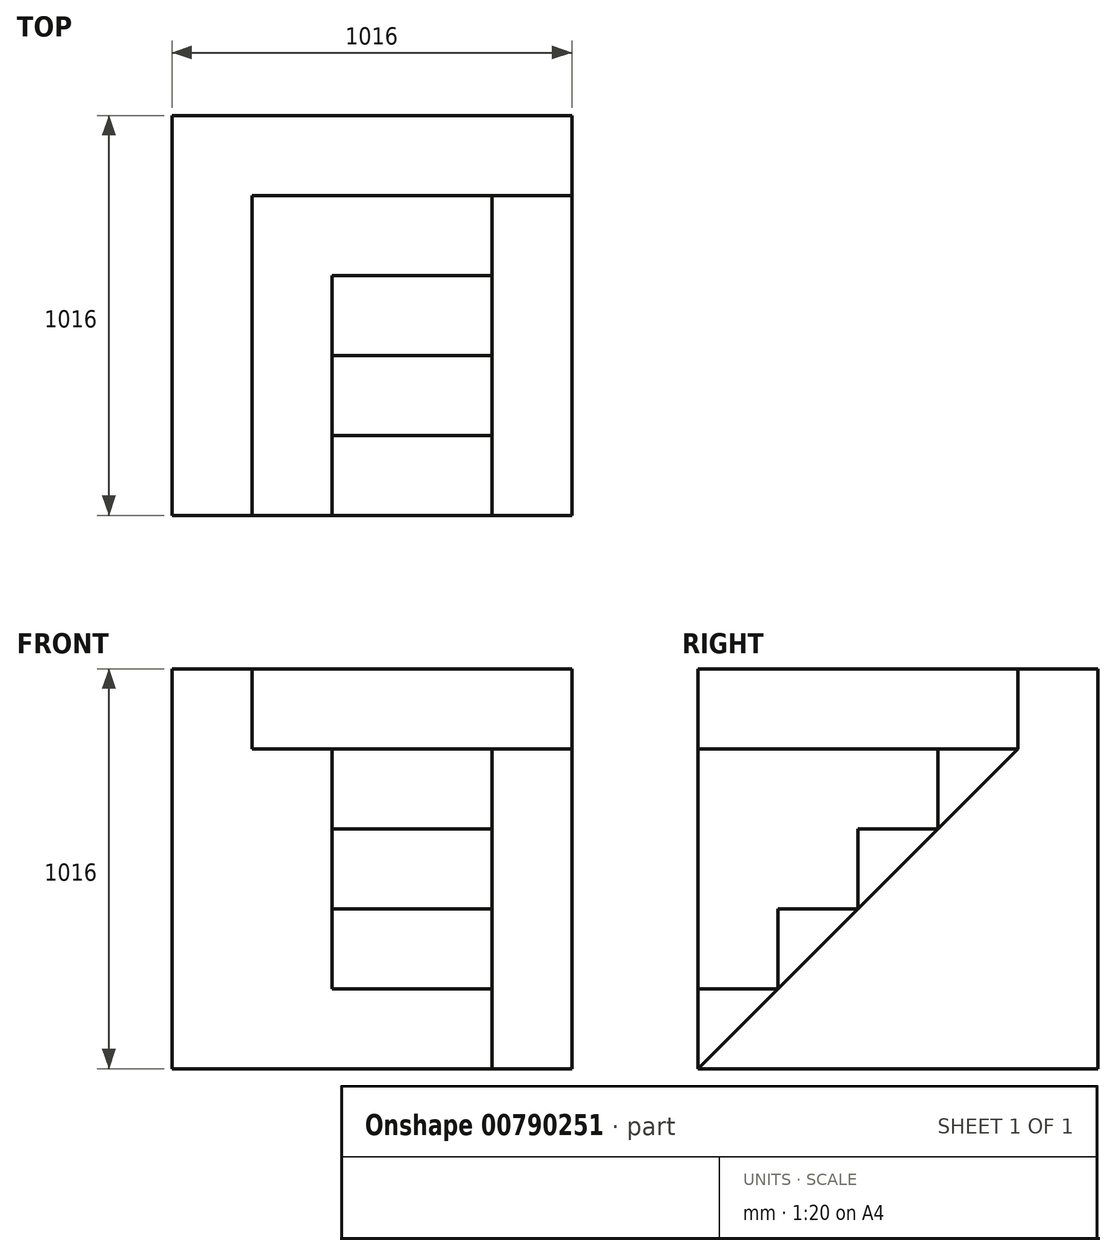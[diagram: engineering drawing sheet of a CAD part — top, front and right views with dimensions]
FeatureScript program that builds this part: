
annotation { "Feature Type Name" : "Feature", "Feature Type Description" : "" }
export const myFeature = defineFeature(function(context is Context, id is Id, definition is map)
    precondition{}
    {
        {
            var Q0;
            Q0=qCreatedBy(makeId("Top.planeOp"),FACE);
            var sketch = newSketch(context, id + "F0", { "sketchPlane" : qUnion([Q0])});
            skLineSegment(sketch, "E0.bottom", {"start": v(-508, -508) * mm, "end": v(508, -508) * mm});
            skLineSegment(sketch, "E0.top", {"start": v(-508, 508) * mm, "end": v(508, 508) * mm});
            skLineSegment(sketch, "E0.left", {"start": v(-508, -508) * mm, "end": v(-508, 508) * mm});
            skLineSegment(sketch, "E0.right", {"start": v(508, -508) * mm, "end": v(508, 508) * mm});
            skLineSegment(sketch, "E1", {"start": v(-304.8, 304.8) * mm, "end": v(-304.8, -508) * mm});
            skLineSegment(sketch, "E2", {"start": v(-304.8, 304.8) * mm, "end": v(508, 304.8) * mm});
            skLineSegment(sketch, "E3", {"start": v(304.8, 304.8) * mm, "end": v(304.8, -508) * mm});
            skLineSegment(sketch, "E4", {"start": v(304.8, 101.6) * mm, "end": v(-101.6, 101.6) * mm});
            skLineSegment(sketch, "E5", {"start": v(-101.6, -101.6) * mm, "end": v(304.8, -101.6) * mm});
            skLineSegment(sketch, "E6", {"start": v(-101.6, -304.8) * mm, "end": v(304.8, -304.8) * mm});
            skLineSegment(sketch, "E7.trimOffspring", {"start": v(-101.6, 101.6) * mm, "end": v(-101.6, -508) * mm});
            skSolve(sketch);
        }
        {
            var Q0;
            {var subQ1=sQuery(id+"F0.wireOp",EDGE,"E0.right");var subQ6=sQuery(id+"F0.wireOp",EDGE,"E0.bottom");var subQ7=makeQuery(id+"F0.imprint","INTERSECT",VERTEX,{"derivedFrom":[subQ6,subQ1]});Q0=makeQuery(id+"F0.imprint","IMPRINT",FACE,{"disambiguationData":[TD([[makeQuery(id+"F0.imprint","IMPRINT",EDGE,{"disambiguationData":[TD([[subQ7,1.0]])],"derivedFrom":subQ6}),1.0]])]});}
            extrude(context, id + "F1", {"entities" : qUnion([Q0]), "depth" : 812.8 * mm, "offsetDistance" : 25.4 * mm});
        }
        {
            var Q0;
            Q0=makeQuery(id+"F1.opExtrude","SWEPT_FACE",FACE,{"disambiguationData":[OSD([sQuery(id+"F0.wireOp",EDGE,"E0.right")])]});
            var sketch = newSketch(context, id + "F2", { "sketchPlane" : qUnion([Q0])});
            skLineSegment(sketch, "E8", {"start": v(-508, 0) * mm, "end": v(304.8, 812.8) * mm});
            skSolve(sketch);
        }
        {
            var Q0;
            Q0=makeQuery(id+"F2.imprint","IMPRINT",FACE,{"disambiguationData":[TD([[makeQuery(id+"F2.imprint","IMPRINT",EDGE,{"derivedFrom":sQuery(id+"F2.wireOp",EDGE,"E8")}),1.0]])]});
            extrude(context, id + "F3", {"entities" : qUnion([Q0]), "operationType" : NewBodyOperationType.REMOVE, "oppositeDirection" : true, "depth" : 16916.4 * mm, "offsetDistance" : 25.4 * mm});
        }
        {
            var Q0;
            {var subQ1=sQuery(id+"F0.wireOp",EDGE,"E0.top");Q0=makeQuery(id+"F0.imprint","IMPRINT",FACE,{"disambiguationData":[TD([[makeQuery(id+"F0.imprint","IMPRINT",EDGE,{"derivedFrom":subQ1}),-1.0]])]});}
            extrude(context, id + "F4", {"entities" : qUnion([Q0]), "operationType" : NewBodyOperationType.ADD, "depth" : 1016 * mm, "offsetDistance" : 25.4 * mm});
        }
        {
            var Q0;
            {var subQ1=sQuery(id+"F0.wireOp",EDGE,"E1");Q0=makeQuery(id+"F0.imprint","IMPRINT",FACE,{"disambiguationData":[TD([[makeQuery(id+"F0.imprint","IMPRINT",EDGE,{"derivedFrom":subQ1}),1.0]])]});}
            extrude(context, id + "F5", {"entities" : qUnion([Q0]), "operationType" : NewBodyOperationType.ADD, "depth" : 812.8 * mm, "offsetDistance" : 25.4 * mm});
        }
        {
            var Q0;
            {var subQ0=sQuery(id+"F0.wireOp",EDGE,"E4");Q0=makeQuery(id+"F0.imprint","IMPRINT",FACE,{"disambiguationData":[TD([[makeQuery(id+"F0.imprint","IMPRINT",EDGE,{"derivedFrom":subQ0}),1.0]])]});}
            extrude(context, id + "F6", {"entities" : qUnion([Q0]), "operationType" : NewBodyOperationType.ADD, "depth" : 609.6 * mm, "offsetDistance" : 25.4 * mm});
        }
        {
            var Q0;
            {var subQ0=sQuery(id+"F0.wireOp",EDGE,"E5");Q0=makeQuery(id+"F0.imprint","IMPRINT",FACE,{"disambiguationData":[TD([[makeQuery(id+"F0.imprint","IMPRINT",EDGE,{"derivedFrom":subQ0}),-1.0]])]});}
            extrude(context, id + "F7", {"entities" : qUnion([Q0]), "operationType" : NewBodyOperationType.ADD, "depth" : 406.4 * mm, "offsetDistance" : 25.4 * mm});
        }
        {
            var Q0;
            {var subQ5=sQuery(id+"F0.wireOp",EDGE,"E6");Q0=makeQuery(id+"F0.imprint","IMPRINT",FACE,{"disambiguationData":[TD([[makeQuery(id+"F0.imprint","IMPRINT",EDGE,{"derivedFrom":subQ5}),-1.0]])]});}
            extrude(context, id + "F8", {"entities" : qUnion([Q0]), "operationType" : NewBodyOperationType.ADD, "depth" : 203.2 * mm, "offsetDistance" : 25.4 * mm});
        }
    });
